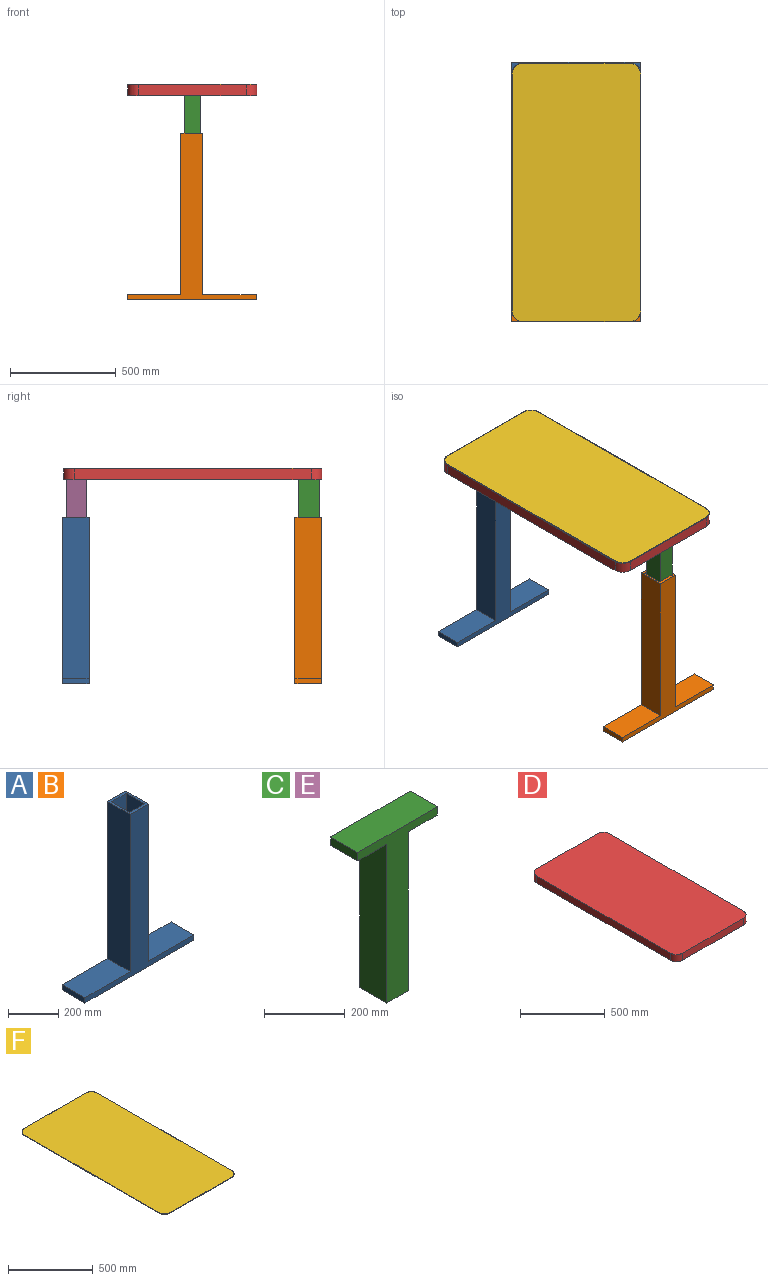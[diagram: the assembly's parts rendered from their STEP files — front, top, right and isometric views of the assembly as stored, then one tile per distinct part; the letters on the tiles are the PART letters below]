
ASSEMBLY  parts=6 mates=5
PART A: 15 faces, bbox 609.6x127x787.4 mm
  f0: plane 127x101.6mm, normal (0,0,1), area 4516.1mm2, adj f2,f4,f8,f9,f10,f11,f12,f13
  f1: plane 254x127mm, normal (0,0,1), area 32258mm2, adj f2,f4,f5,f8
  f2: plane 787.4x609.6mm, normal (0,1,0), area 92903mm2, adj f0,f1,f3,f5,f6,f7,f8,f9
  f3: plane 127x25.4mm, normal (-1,0,0), area 3225.8mm2, adj f2,f4,f6,f7
  f4: plane 787.4x609.6mm, normal (0,-1,0), area 92903mm2, adj f0,f1,f3,f5,f6,f7,f8,f9
  f5: plane 127x25.4mm, normal (1,0,0), area 3225.8mm2, adj f1,f2,f4,f7
  f6: plane 254x127mm, normal (0,0,1), area 32258mm2, adj f2,f3,f4,f9
  f7: plane 609.6x127mm, normal (0,0,-1), area 77419.2mm2, adj f2,f3,f4,f5
  f8: plane 762x127mm, normal (1,0,0), area 96774mm2, adj f0,f1,f2,f4
  f9: plane 762x127mm, normal (-1,0,0), area 96774mm2, adj f0,f2,f4,f6
  f10: plane 736.6x82.55mm, normal (0,1,0), area 60806.3mm2, adj f0,f11,f13,f14
  f11: plane 736.6x101.6mm, normal (-1,0,0), area 74838.6mm2, adj f0,f10,f12,f14
  f12: plane 736.6x82.55mm, normal (0,-1,0), area 60806.3mm2, adj f0,f11,f13,f14
  f13: plane 736.6x101.6mm, normal (1,0,0), area 74838.6mm2, adj f0,f10,f12,f14
  f14: plane 101.6x82.55mm, normal (0,0,1), area 8387.1mm2, adj f10,f11,f12,f13
PART B: same geometry as A
PART C: 10 faces, bbox 279.4x95.3x508 mm
  f0: plane 482.6x95.25mm, normal (1,0,0), area 45967.7mm2, adj f1,f2,f5,f6
  f1: plane 508x279.4mm, normal (0,-1,0), area 43870.9mm2, adj f0,f3,f4,f5,f6,f7,f8,f9
  f2: plane 508x279.4mm, normal (0,1,0), area 43870.9mm2, adj f0,f3,f4,f5,f6,f7,f8,f9
  f3: plane 482.6x95.25mm, normal (-1,0,0), area 45967.7mm2, adj f1,f2,f5,f8
  f4: plane 279.4x95.25mm, normal (0,0,1), area 26612.9mm2, adj f1,f2,f7,f9
  f5: plane 95.25x76.2mm, normal (0,0,-1), area 7258mm2, adj f0,f1,f2,f3
  f6: plane 101.6x95.25mm, normal (0,0,-1), area 9677.4mm2, adj f0,f1,f2,f7
  f7: plane 95.25x25.4mm, normal (1,0,0), area 2419.4mm2, adj f1,f2,f4,f6
  f8: plane 101.6x95.25mm, normal (0,0,-1), area 9677.4mm2, adj f1,f2,f3,f9
  f9: plane 95.25x25.4mm, normal (-1,0,0), area 2419.4mm2, adj f1,f2,f4,f8
PART D: 19 faces, bbox 609.6x1219.2x50.8 mm
  f0: plane 508x50.8mm, normal (0,1,0), area 25806.4mm2, adj f1,f7,f8,f9
  f1: cylinder r=50.8mm len=50.8mm, axis (0,0,1), area 4053.7mm2, adj f0,f2,f8,f9
  f2: plane 1117.6x50.8mm, normal (-1,0,0), area 56774.1mm2, adj f1,f3,f8,f9
  f3: cylinder r=50.8mm len=50.8mm, axis (0,0,1), area 4053.7mm2, adj f2,f4,f8,f9
  f4: plane 508x50.8mm, normal (0,-1,0), area 25806.4mm2, adj f3,f5,f8,f9
  f5: cylinder r=50.8mm len=50.8mm, axis (0,0,1), area 4053.7mm2, adj f4,f6,f8,f9
  f6: plane 1117.6x50.8mm, normal (1,0,0), area 56774.1mm2, adj f5,f7,f8,f9
  f7: cylinder r=50.8mm len=50.8mm, axis (0,0,1), area 4053.7mm2, adj f0,f6,f8,f9
  f8: plane 1219.2x609.6mm, normal (0,0,-1), area 44837.2mm2, adj f0,f1,f2,f3,f4,f5,f6,f7
  f9: plane 1219.2x609.6mm, normal (0,0,1), area 741009.1mm2, adj f0,f1,f2,f3,f4,f5,f6,f7
  f10: plane 508x38.1mm, normal (0,-1,0), area 19354.8mm2, adj f8,f11,f17,f18
  f11: cylinder r=38.1mm len=38.1mm, axis (0,0,1), area 2280.2mm2, adj f8,f10,f12,f18
  f12: plane 1117.6x38.1mm, normal (1,0,0), area 42580.6mm2, adj f8,f11,f13,f18
  f13: cylinder r=38.1mm len=38.1mm, axis (0,0,1), area 2280.2mm2, adj f8,f12,f14,f18
  f14: plane 508x38.1mm, normal (0,1,0), area 19354.8mm2, adj f8,f13,f15,f18
  f15: cylinder r=38.1mm len=38.1mm, axis (0,0,1), area 2280.2mm2, adj f8,f14,f16,f18
  f16: plane 1117.6x38.1mm, normal (-1,0,0), area 42580.6mm2, adj f8,f15,f17,f18
  f17: cylinder r=38.1mm len=38.1mm, axis (0,0,1), area 2280.2mm2, adj f8,f10,f16,f18
  f18: plane 1193.8x584.2mm, normal (0,0,-1), area 696171.9mm2, adj f10,f11,f12,f13,f14,f15,f16,f17
PART E: same geometry as C
PART F: 26 faces, bbox 618x1227.6x3.2 mm
  f0: plane 508x0.64mm, normal (0,1,0), area 322.6mm2, adj f1,f7,f13,f21
  f1: cylinder r=50.8mm len=50.8mm, axis (0,0,-1), area 50.7mm2, adj f0,f2,f15,f23
  f2: plane 1117.6x0.64mm, normal (-1,0,0), area 709.7mm2, adj f1,f3,f17,f25
  f3: cylinder r=50.8mm len=50.8mm, axis (0,0,-1), area 50.7mm2, adj f2,f4,f16,f24
  f4: plane 508x0.64mm, normal (0,-1,0), area 322.6mm2, adj f3,f5,f14,f22
  f5: cylinder r=50.8mm len=50.8mm, axis (0,0,-1), area 50.7mm2, adj f4,f6,f12,f20
  f6: plane 1117.6x0.64mm, normal (1,0,0), area 709.7mm2, adj f5,f7,f10,f18
  f7: cylinder r=50.8mm len=50.8mm, axis (0,0,-1), area 50.7mm2, adj f0,f6,f11,f19
  f8: plane 1216.66x607.06mm, normal (0,0,1), area 736479.8mm2, adj f18,f19,f20,f21,f22,f23,f24,f25
  f9: plane 1216.66x607.06mm, normal (0,0,-1), area 736479.8mm2, adj f10,f11,f12,f13,f14,f15,f16,f17
  f10: cylinder r=1.27mm len=1117.6mm, axis (0,1,0), area 2229.5mm2, adj f6,f9,f11,f12
  f11: torus R=49.53mm, axis (0,0,1), area 157.7mm2, adj f7,f9,f10,f13
  f12: torus R=49.53mm, axis (0,0,1), area 157.7mm2, adj f5,f9,f10,f14
  f13: cylinder r=1.27mm len=508mm, axis (-1,0,0), area 1013.4mm2, adj f0,f9,f11,f15
  f14: cylinder r=1.27mm len=508mm, axis (1,0,0), area 1013.4mm2, adj f4,f9,f12,f16
  f15: torus R=49.53mm, axis (0,0,1), area 157.7mm2, adj f1,f9,f13,f17
  f16: torus R=49.53mm, axis (0,0,1), area 157.7mm2, adj f3,f9,f14,f17
  f17: cylinder r=1.27mm len=1117.6mm, axis (0,-1,0), area 2229.5mm2, adj f2,f9,f15,f16
  f18: cylinder r=1.27mm len=1117.6mm, axis (0,-1,0), area 2229.5mm2, adj f6,f8,f19,f20
  f19: torus R=49.53mm, axis (0,0,1), area 157.7mm2, adj f7,f8,f18,f21
  f20: torus R=49.53mm, axis (0,0,1), area 157.7mm2, adj f5,f8,f18,f22
  f21: cylinder r=1.27mm len=508mm, axis (1,0,0), area 1013.4mm2, adj f0,f8,f19,f23
  f22: cylinder r=1.27mm len=508mm, axis (-1,0,0), area 1013.4mm2, adj f4,f8,f20,f24
  f23: torus R=49.53mm, axis (0,0,1), area 157.7mm2, adj f1,f8,f21,f25
  f24: torus R=49.53mm, axis (0,0,1), area 157.7mm2, adj f3,f8,f22,f25
  f25: cylinder r=1.27mm len=1117.6mm, axis (0,1,0), area 2229.5mm2, adj f2,f8,f23,f24
PLACE A t=(470.21,1354.81,-997.66)mm
PLACE B t=(470.21,256.26,-997.66)mm
PLACE C t=(778.19,189.59,-502.72)mm
PLACE D t=(778.19,738.86,17.98)mm
PLACE E t=(778.19,1288.14,-502.72)mm
PLACE F t=(778.19,738.86,17.98)mm
MATE fastened F.f9 <-> D.f9  axis (0,0,-1) through (778.19,738.86,17.98)mm
MATE fastened E.f4 <-> D.f18  axis (0,0,1) through (778.19,1335.76,5.28)mm
MATE slider C.f6 <-> B.f0  axis (0,0,-1) through (816.29,141.96,-20.12)mm
MATE fastened C.f4 <-> D.f18  axis (0,0,1) through (778.19,141.96,5.28)mm
MATE slider E.f6 <-> A.f0  axis (0,0,-1) through (816.29,1240.51,-20.12)mm
